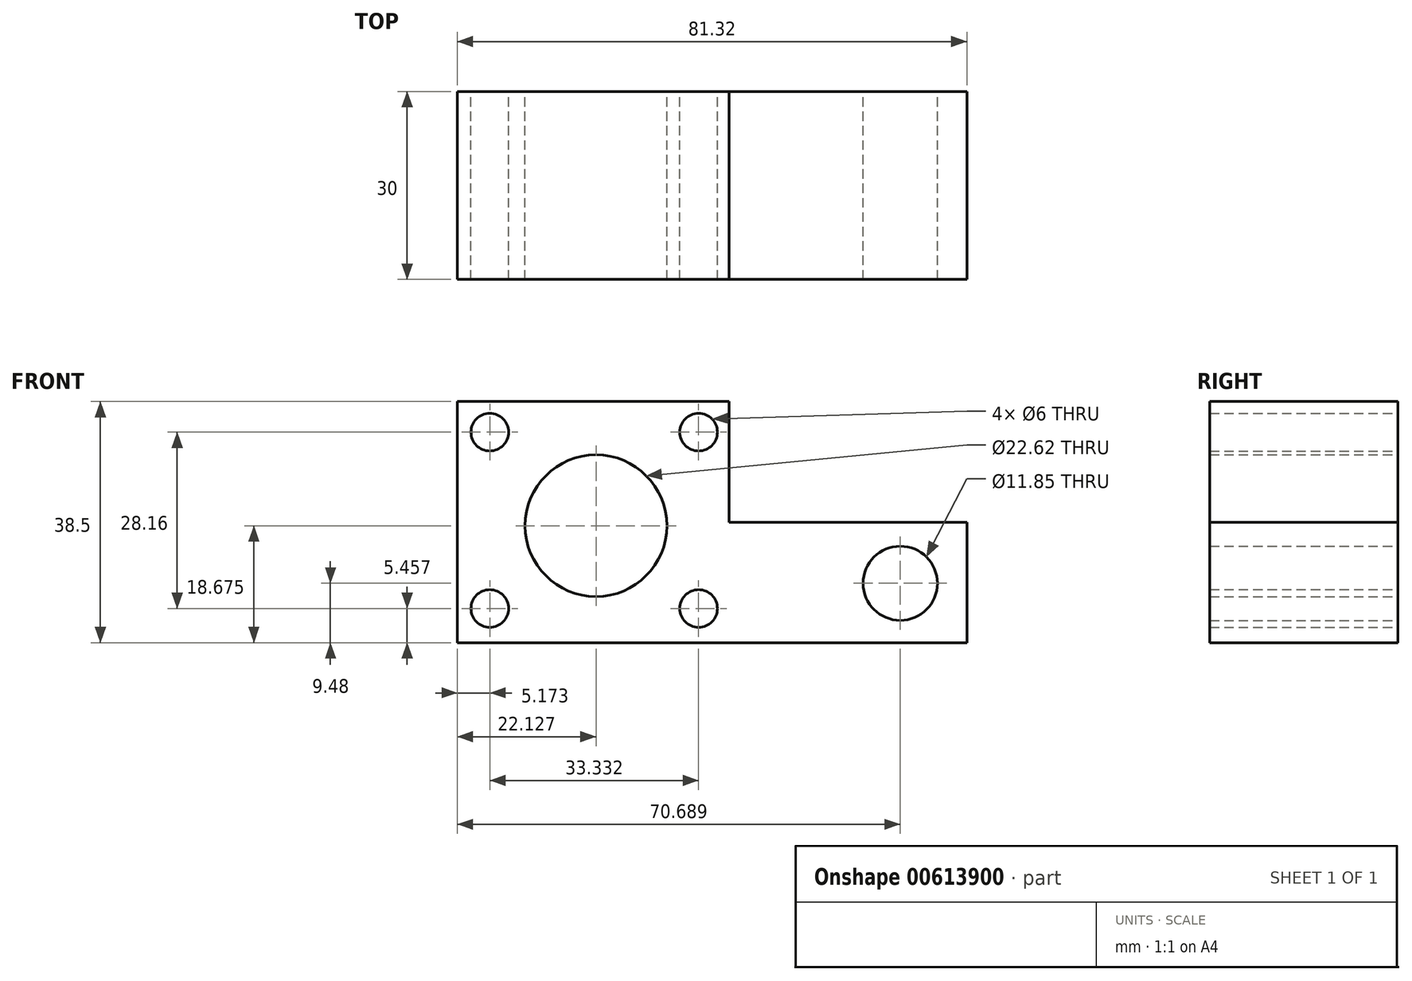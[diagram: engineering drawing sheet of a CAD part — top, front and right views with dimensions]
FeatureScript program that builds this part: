
annotation { "Feature Type Name" : "Feature", "Feature Type Description" : "" }
export const myFeature = defineFeature(function(context is Context, id is Id, definition is map)
    precondition{}
    {
        {
            var Q0;
            Q0=qCreatedBy(makeId("Front.planeOp"),FACE);
            var sketch = newSketch(context, id + "F0", { "sketchPlane" : qUnion([Q0])});
            skLineSegment(sketch, "E0.bottom", {"start": v(-51.58, 29.02) * mm, "end": v(-8.19, 29.02) * mm});
            skLineSegment(sketch, "E0.top", {"start": v(-51.58, -9.48) * mm, "end": v(-8.19, -9.48) * mm});
            skLineSegment(sketch, "E0.left", {"start": v(-51.58, 29.02) * mm, "end": v(-51.58, -9.48) * mm});
            skLineSegment(sketch, "E0.right", {"start": v(-8.19, 29.02) * mm, "end": v(-8.19, 9.77) * mm});
            skPoint(sketch, "E1.oppositeSnap0", {"position": v(-8.19, 9.77) * mm});
            skLineSegment(sketch, "E1.bottom", {"start": v(-8.19, -9.48) * mm, "end": v(29.74, -9.48) * mm});
            skLineSegment(sketch, "E1.top", {"start": v(-8.19, 9.77) * mm, "end": v(29.74, 9.77) * mm});
            skLineSegment(sketch, "E1.right", {"start": v(29.74, -9.48) * mm, "end": v(29.74, 9.77) * mm});
            skCircle(sketch, "E2", {"center": v(-46.4, 24.14) * mm, "radius": 3 * mm});
            skCircle(sketch, "E3", {"center": v(-13.07, 24.14) * mm, "radius": 3 * mm});
            skCircle(sketch, "E4", {"center": v(-13.07, -4.02) * mm, "radius": 3 * mm});
            skCircle(sketch, "E5", {"center": v(-46.4, -4.02) * mm, "radius": 3 * mm});
            skCircle(sketch, "E6", {"center": v(-29.45, 9.2) * mm, "radius": 11.3 * mm});
            skCircle(sketch, "E7", {"center": v(19.1, 0) * mm, "radius": 5.92 * mm});
            skSolve(sketch);
        }
        {
            var Q0;
            Q0 = qSketchRegion(id + "F0", true);
            extrude(context, id + "F1", {"entities" : qUnion([Q0]), "depth" : 30 * mm, "offsetDistance" : 25 * mm});
        }
    });
